# Revit family: QF_BOURGEAT_Chariots_à_plateaux_Démontables
name_source: partatom
category: Equipement spécialisé
revit_build: Autodesk Revit 2015 (Build: 20140606_1530(x64)
units: mm (PartAtom-declared; Revit-internal decimal feet)

## types (6) — shared parameters
Certification = NF Hygiène Alimentaire
Charge maxi = 50 Kg par plateau
Fabricant = BOURGEAT
Spécification du Fabricant = Chariot à plateaux démontables
URL catalogue = http://www.bourgeat.fr

## per-type parameters (varying)
| type | Charge max | Decal barreau | Decal guéridon | Espace entre les plateaux | Galerie | Guéridon | Hauteur echelle | Hauteur hors tout | Largeur galerie | Largeur plateau | Longueur galerie | Longueur hors tout | Longueur plateau | Modèle | Plateaux | Position perçage Lar | Position perçage long | Profondeur echelle | Profondeur hors tout |
| Plateau 900x550 - Modèle 2 plateaux | 100.00 kg | 60 mm  [stored 0.19685 ft] | 98 mm | 590 mm  [stored 1.9357 ft] | Non | Non | 801 mm | 960 mm | 465 mm  [stored 1.52559 ft] | 550 mm  [stored 1.80446 ft] | 805 mm  [stored 2.64108 ft] | 940 mm  [stored 3.08399 ft] | 900 mm  [stored 2.95276 ft] | 778156 | 2 | 500 mm  [stored 1.64042 ft] | 840 mm  [stored 2.75591 ft] | 522 mm | 600 mm |
| Plateau 900x550 - Modèle 3 plateaux | 150.00 kg | 60 mm  [stored 0.19685 ft] | 98 mm | 280 mm  [stored 0.918635 ft] | Non | Non | 801 mm | 960 mm | 555 mm  [stored 1.82087 ft] | 640 mm  [stored 2.09974 ft] | 845 mm  [stored 2.77231 ft] | 980 mm | 940 mm  [stored 3.08399 ft] | 778556 | 3 | 590 mm  [stored 1.9357 ft] | 880 mm  [stored 2.88714 ft] | 612 mm  [stored 2.00787 ft] | 690 mm  [stored 2.26378 ft] |
| Plateau 800x500 - Modèle 2 plateaux | 100.00 kg | 60 mm  [stored 0.19685 ft] | 98 mm | 590 mm  [stored 1.9357 ft] | Non | Non | 801 mm | 960 mm | 415 mm  [stored 1.36155 ft] | 500 mm  [stored 1.64042 ft] | 705 mm  [stored 2.31299 ft] | 840 mm  [stored 2.75591 ft] | 800 mm  [stored 2.62467 ft] | 778056 | 2 | 450 mm  [stored 1.47638 ft] | 740 mm  [stored 2.42782 ft] | 472 mm | 550 mm  [stored 1.80446 ft] |
| Plateau 800x500 - Modèle 3 plateaux | 150.00 kg | 60 mm  [stored 0.19685 ft] | 98 mm | 280 mm  [stored 0.918635 ft] | Non | Non | 801 mm | 960 mm | 415 mm  [stored 1.36155 ft] | 500 mm  [stored 1.64042 ft] | 705 mm  [stored 2.31299 ft] | 840 mm  [stored 2.75591 ft] | 800 mm  [stored 2.62467 ft] | 778456 | 3 | 450 mm  [stored 1.47638 ft] | 740 mm  [stored 2.42782 ft] | 472 mm | 550 mm  [stored 1.80446 ft] |
| Guéridon 600x400 - Modèle 2 plateaux - Avec galerie | 100.00 kg | 60 mm  [stored 0.19685 ft] | 50 mm  [stored 0.164042 ft] | 590 mm  [stored 1.9357 ft] | Oui | Oui | 746 mm | 905 mm  [stored 2.96916 ft] | 325 mm  [stored 1.06627 ft] | 400 mm  [stored 1.31234 ft] | 525 mm | 660 mm | 600 mm | 778316 | 2 | 360 mm  [stored 1.1811 ft] | 560 mm | 382 mm  [stored 1.25328 ft] | 460 mm  [stored 1.50919 ft] |
| Guéridon 600x400 - Modèle 2 plateaux - Sans galerie | 100.00 kg | 10 mm  [stored 0.0328084 ft] | 0 mm  [stored 0 ft] | 590 mm  [stored 1.9357 ft] | Non | Oui | 686 mm | 845 mm  [stored 2.77231 ft] | 325 mm  [stored 1.06627 ft] | 400 mm  [stored 1.31234 ft] | 525 mm | 660 mm | 600 mm | 778306 | 2 | 360 mm  [stored 1.1811 ft] | 560 mm | 382 mm  [stored 1.25328 ft] | 460 mm  [stored 1.50919 ft] |

note: [stored X ft] marks values corroborated as IEEE doubles in the binary element streams (Revit-internal decimal feet)
